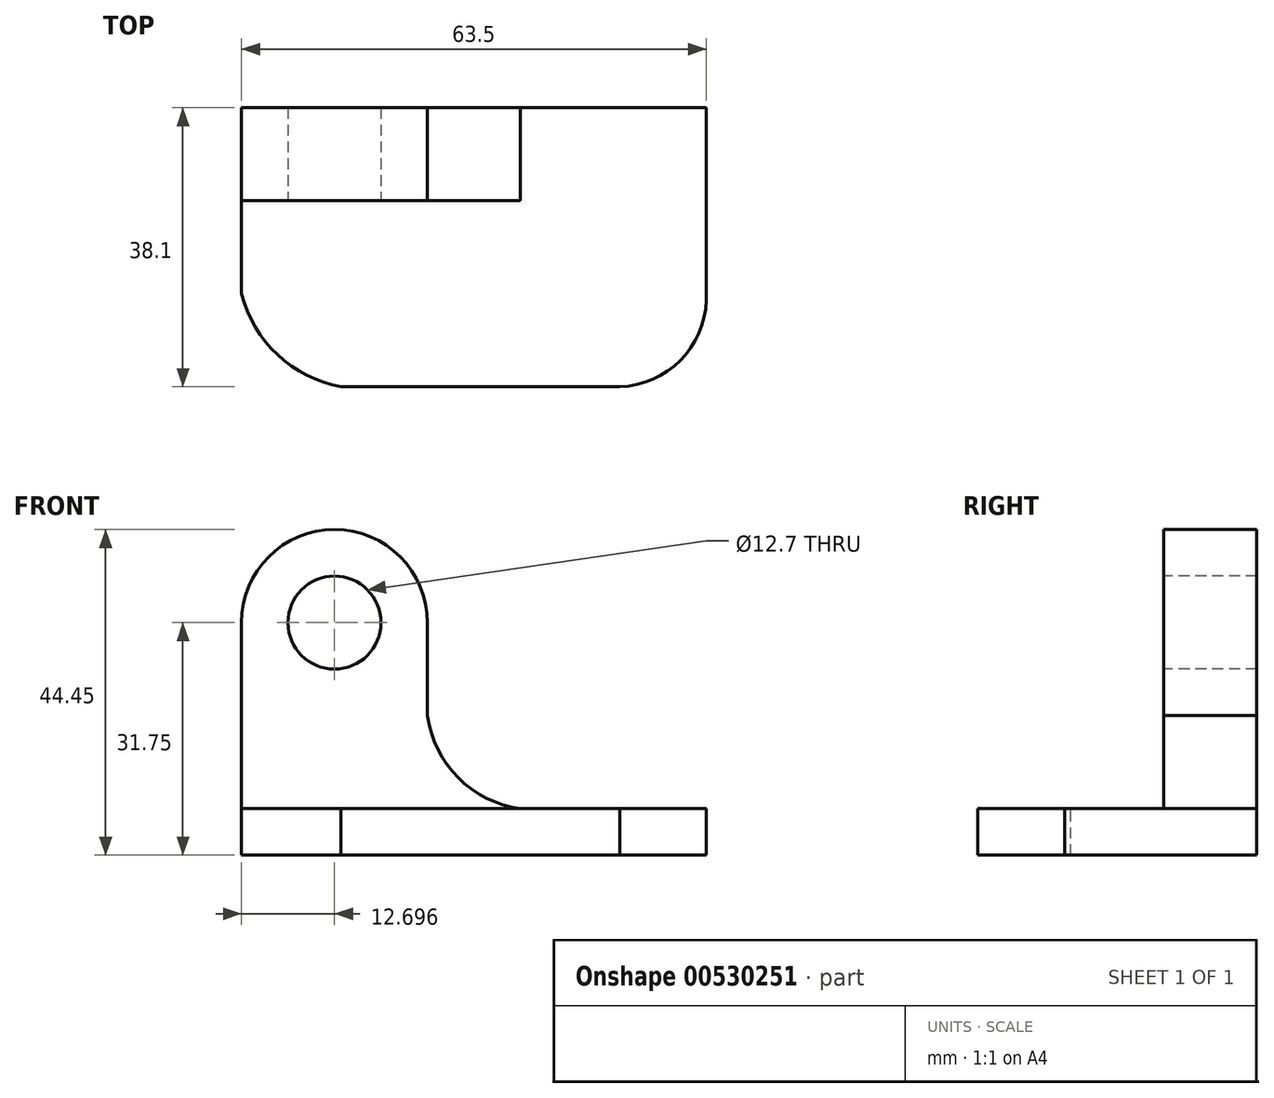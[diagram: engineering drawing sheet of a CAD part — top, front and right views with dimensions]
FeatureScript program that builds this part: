
annotation { "Feature Type Name" : "Feature", "Feature Type Description" : "" }
export const myFeature = defineFeature(function(context is Context, id is Id, definition is map)
    precondition{}
    {
        {
            var Q0;
            Q0=qCreatedBy(makeId("Front.planeOp"),FACE);
            var sketch = newSketch(context, id + "F0", { "sketchPlane" : qUnion([Q0])});
            skLineSegment(sketch, "E0", {"start": v(-87.21, 0) * mm, "end": v(-23.71, 0) * mm});
            skLineSegment(sketch, "E1", {"start": v(-23.71, 0) * mm, "end": v(-23.71, 6.35) * mm});
            skLineSegment(sketch, "E2", {"start": v(-23.71, 6.35) * mm, "end": v(-87.21, 6.35) * mm});
            skLineSegment(sketch, "E3", {"start": v(-87.21, 6.35) * mm, "end": v(-87.21, 0) * mm});
            skSolve(sketch);
        }
        {
            var Q0;
            Q0 = qSketchRegion(id + "F0", true);
            extrude(context, id + "F1", {"entities" : qUnion([Q0]), "depth" : 38.1 * mm, "offsetDistance" : 25.4 * mm});
        }
        {
            var Q0;
            Q0=makeQuery(id+"F1.opExtrude","SWEPT_FACE",FACE,{"disambiguationData":[OSD([sQuery(id+"F0.wireOp",EDGE,"E2")])]});
            var sketch = newSketch(context, id + "F2", { "sketchPlane" : qUnion([Q0])});
            skArc(sketch, "E4", {"start": v(-36.41, -38.1) * mm, "mid": v(-27.3, -34.52) * mm, "end": v(-23.71, -25.4) * mm});
            skSolve(sketch);
        }
        {
            var Q0;
            {var subQ0=sQuery(id+"F2.wireOp",EDGE,"E4");var subQ1=sQuery(id+"F0.wireOp",EDGE,"E2");var subQ2=makeQuery(id+"F1.opExtrude","CAP_EDGE",EDGE,{"disambiguationData":[OSD([subQ1])],"isStart":false});var subQ3=makeQuery(id+"F2.imprint","INTERSECT",VERTEX,{"disambiguationData":[OD(1.0)],"derivedFrom":[subQ2,subQ0]});Q0=makeQuery(id+"F2.imprint","IMPRINT",FACE,{"disambiguationData":[TD([[makeQuery(id+"F2.imprint","IMPRINT",EDGE,{"disambiguationData":[TD([[subQ3,-1.0]])],"derivedFrom":subQ0}),-1.0]])]});}
            extrude(context, id + "F3", {"entities" : qUnion([Q0]), "operationType" : NewBodyOperationType.REMOVE, "oppositeDirection" : true, "depth" : 25.4 * mm, "offsetDistance" : 25.4 * mm});
        }
        {
            var Q0;
            Q0=makeQuery(id+"F1.opExtrude","SWEPT_FACE",FACE,{"disambiguationData":[OSD([sQuery(id+"F0.wireOp",EDGE,"E2")])]});
            var sketch = newSketch(context, id + "F4", { "sketchPlane" : qUnion([Q0])});
            skArc(sketch, "E5", {"start": v(-87.21, -25.4) * mm, "mid": v(-82.28, -33.73) * mm, "end": v(-73.63, -38.1) * mm});
            skSolve(sketch);
        }
        {
            var Q0;
            {var subQ0=sQuery(id+"F4.wireOp",EDGE,"E5");Q0=makeQuery(id+"F4.imprint","IMPRINT",FACE,{"disambiguationData":[TD([[makeQuery(id+"F4.imprint","IMPRINT",EDGE,{"derivedFrom":subQ0}),-1.0]])]});}
            extrude(context, id + "F5", {"entities" : qUnion([Q0]), "operationType" : NewBodyOperationType.REMOVE, "oppositeDirection" : true, "depth" : 25.4 * mm, "offsetDistance" : 25.4 * mm});
        }
        {
            var Q0;
            Q0=makeQuery(id+"F1.opExtrude","CAP_FACE",FACE,{"disambiguationData":[OSD([sQuery(id+"F0.wireOp",EDGE,"E0"),sQuery(id+"F0.wireOp",EDGE,"E1"),sQuery(id+"F0.wireOp",EDGE,"E2"),sQuery(id+"F0.wireOp",EDGE,"E3")])],"isStart":true});
            var sketch = newSketch(context, id + "F6", { "sketchPlane" : qUnion([Q0])});
            skLineSegment(sketch, "E6", {"start": v(61.81, 6.35) * mm, "end": v(61.81, 31.75) * mm});
            skLineSegment(sketch, "E7", {"start": v(61.81, 31.75) * mm, "end": v(87.21, 31.75) * mm});
            skLineSegment(sketch, "E8", {"start": v(87.21, 31.75) * mm, "end": v(87.21, 6.35) * mm});
            skLineSegment(sketch, "E9", {"start": v(87.21, 6.35) * mm, "end": v(61.81, 6.35) * mm});
            skSolve(sketch);
        }
        {
            var Q0;
            Q0=makeQuery(id+"F6.imprint","IMPRINT",FACE,{"disambiguationData":[TD([[makeQuery(id+"F6.imprint","IMPRINT",EDGE,{"derivedFrom":sQuery(id+"F6.wireOp",EDGE,"E6")}),-1.0]])]});
            extrude(context, id + "F7", {"entities" : qUnion([Q0]), "operationType" : NewBodyOperationType.ADD, "oppositeDirection" : true, "depth" : 12.7 * mm, "offsetDistance" : 25.4 * mm});
        }
        {
            var Q0;
            Q0=makeQuery(id+"F7.boolean.opBoolean","MERGE",FACE,{"derivedFrom":[makeQuery(id+"F1.opExtrude","CAP_FACE",FACE,{"disambiguationData":[OSD([sQuery(id+"F0.wireOp",EDGE,"E0"),sQuery(id+"F0.wireOp",EDGE,"E1"),sQuery(id+"F0.wireOp",EDGE,"E2"),sQuery(id+"F0.wireOp",EDGE,"E3")])],"isStart":true}),makeQuery(id+"F7.opExtrude","CAP_FACE",FACE,{"disambiguationData":[OSD([sQuery(id+"F6.wireOp",EDGE,"E6"),sQuery(id+"F6.wireOp",EDGE,"E7"),sQuery(id+"F6.wireOp",EDGE,"E8"),sQuery(id+"F6.wireOp",EDGE,"E9")])],"isStart":true})]});
            var sketch = newSketch(context, id + "F8", { "sketchPlane" : qUnion([Q0])});
            skArc(sketch, "E10", {"start": v(49.11, 6.35) * mm, "mid": v(57.6, 10.57) * mm, "end": v(61.81, 19.05) * mm});
            skSolve(sketch);
        }
        {
            var Q0;
            Q0 = qSketchRegion(id + "F8", true);
            var Q1;
            {var subQ0=sQuery(id+"F8.wireOp",EDGE,"E10");Q1=makeQuery(id+"F8.imprint","IMPRINT",FACE,{"disambiguationData":[TD([[makeQuery(id+"F8.imprint","IMPRINT",EDGE,{"derivedFrom":subQ0}),-1.0]])]});}
            extrude(context, id + "F9", {"entities" : qUnion([Q0, Q1]), "operationType" : NewBodyOperationType.ADD, "oppositeDirection" : true, "depth" : 12.7 * mm, "offsetDistance" : 25.4 * mm});
        }
        {
            var Q0;
            {var subQ0=sQuery(id+"F6.wireOp",EDGE,"E6");var subQ1=sQuery(id+"F0.wireOp",EDGE,"E2");Q0=makeQuery(id+"F9.boolean.opBoolean","MERGE",FACE,{"derivedFrom":[makeQuery(id+"F7.boolean.opBoolean","MERGE",FACE,{"derivedFrom":[makeQuery(id+"F1.opExtrude","CAP_FACE",FACE,{"disambiguationData":[OSD([sQuery(id+"F0.wireOp",EDGE,"E0"),sQuery(id+"F0.wireOp",EDGE,"E1"),subQ1,sQuery(id+"F0.wireOp",EDGE,"E3")])],"isStart":true}),makeQuery(id+"F7.opExtrude","CAP_FACE",FACE,{"disambiguationData":[OSD([subQ0,sQuery(id+"F6.wireOp",EDGE,"E7"),sQuery(id+"F6.wireOp",EDGE,"E8"),sQuery(id+"F6.wireOp",EDGE,"E9")])],"isStart":true})]}),makeQuery(id+"F9.opExtrude","CAP_FACE",FACE,{"disambiguationData":[OSD([subQ1,subQ0,sQuery(id+"F8.wireOp",EDGE,"E10")])],"isStart":true})]});}
            var sketch = newSketch(context, id + "F10", { "sketchPlane" : qUnion([Q0])});
            skArc(sketch, "E11", {"start": v(87.21, 31.75) * mm, "mid": v(74.51, 44.45) * mm, "end": v(61.81, 31.75) * mm});
            skSolve(sketch);
        }
        {
            var Q0;
            Q0=makeQuery(id+"F10.imprint","IMPRINT",FACE,{"disambiguationData":[TD([[makeQuery(id+"F10.imprint","IMPRINT",EDGE,{"derivedFrom":sQuery(id+"F10.wireOp",EDGE,"E11")}),1.0]])]});
            extrude(context, id + "F11", {"entities" : qUnion([Q0]), "operationType" : NewBodyOperationType.ADD, "oppositeDirection" : true, "depth" : 12.7 * mm, "offsetDistance" : 25.4 * mm});
        }
        {
            var Q0;
            {var subQ0=sQuery(id+"F6.wireOp",EDGE,"E7");var subQ1=sQuery(id+"F6.wireOp",EDGE,"E6");Q0=makeQuery(id+"F11.boolean.opBoolean","MERGE",FACE,{"derivedFrom":[makeQuery(id+"F9.boolean.opBoolean","MERGE",FACE,{"derivedFrom":[makeQuery(id+"F7.opExtrude","CAP_FACE",FACE,{"disambiguationData":[OSD([subQ1,subQ0,sQuery(id+"F6.wireOp",EDGE,"E8"),sQuery(id+"F6.wireOp",EDGE,"E9")])],"isStart":false}),makeQuery(id+"F9.opExtrude","CAP_FACE",FACE,{"disambiguationData":[OSD([sQuery(id+"F0.wireOp",EDGE,"E2"),subQ1,sQuery(id+"F8.wireOp",EDGE,"E10")])],"isStart":false})]}),makeQuery(id+"F11.opExtrude","CAP_FACE",FACE,{"disambiguationData":[OSD([subQ0,sQuery(id+"F10.wireOp",EDGE,"E11")])],"isStart":false})]});}
            var sketch = newSketch(context, id + "F12", { "sketchPlane" : qUnion([Q0])});
            skCircle(sketch, "E12", {"center": v(-74.51, 31.75) * mm, "radius": 6.35 * mm});
            skSolve(sketch);
        }
        {
            var Q0;
            Q0=makeQuery(id+"F12.imprint","IMPRINT",FACE,{"disambiguationData":[TD([[makeQuery(id+"F12.imprint","IMPRINT",EDGE,{"derivedFrom":sQuery(id+"F12.wireOp",EDGE,"E12")}),1.0]])]});
            extrude(context, id + "F13", {"entities" : qUnion([Q0]), "operationType" : NewBodyOperationType.REMOVE, "oppositeDirection" : true, "depth" : 25.4 * mm, "offsetDistance" : 25.4 * mm});
        }
    });
